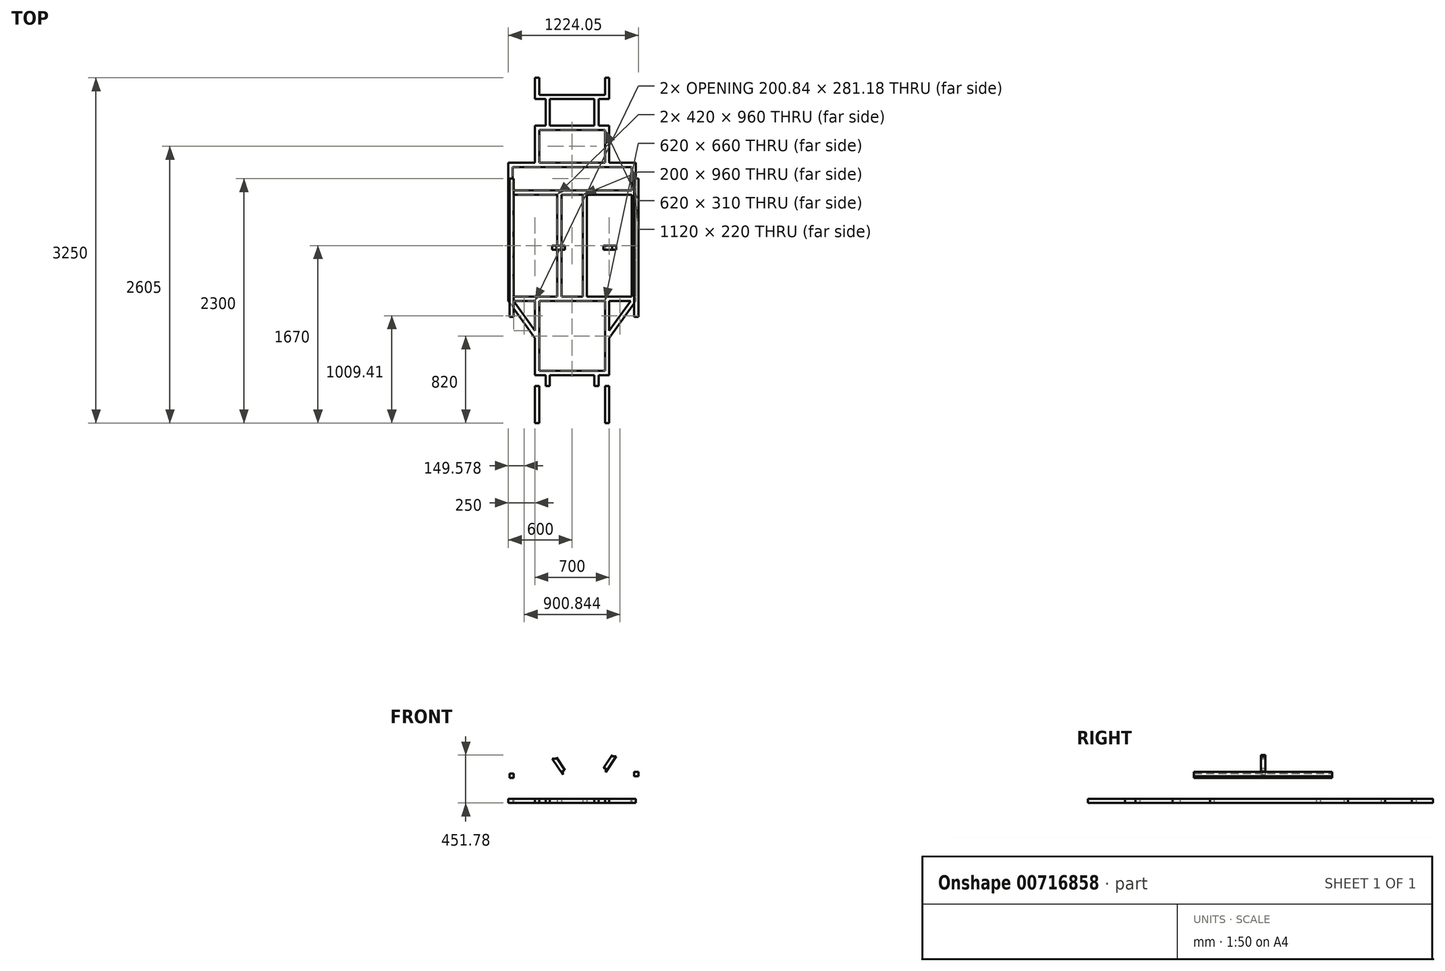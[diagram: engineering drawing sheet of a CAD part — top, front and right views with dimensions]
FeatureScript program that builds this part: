
annotation { "Feature Type Name" : "Feature", "Feature Type Description" : "" }
export const myFeature = defineFeature(function(context is Context, id is Id, definition is map)
    precondition{}
    {
        {
            var Q0;
            Q0=qCreatedBy(makeId("Top.planeOp"),FACE);
            var sketch = newSketch(context, id + "F0", { "sketchPlane" : qUnion([Q0])});
            skLineSegment(sketch, "E0.bottom", {"start": v(100, 500) * mm, "end": v(-100, 500) * mm});
            skLineSegment(sketch, "E0.top", {"start": v(100, -500) * mm, "end": v(-100, -500) * mm});
            skLineSegment(sketch, "E0.right", {"start": v(-100, 500) * mm, "end": v(-100, -460) * mm});
            skPoint(sketch, "E0.middle", {"position": v(0, 0) * mm});
            skLineSegment(sketch, "E1.bottom", {"start": v(140, 500) * mm, "end": v(600, 500) * mm});
            skLineSegment(sketch, "E1.top", {"start": v(100, -500) * mm, "end": v(310, -500) * mm});
            skLineSegment(sketch, "E1.right", {"start": v(600, 500) * mm, "end": v(600, -500) * mm});
            skLineSegment(sketch, "E2.bottom", {"start": v(-140, 500) * mm, "end": v(-560, 500) * mm});
            skLineSegment(sketch, "E2.top", {"start": v(-100, -500) * mm, "end": v(-550.84, -500) * mm});
            skLineSegment(sketch, "E2.right", {"start": v(-600, 500) * mm, "end": v(-600, -500) * mm});
            skLineSegment(sketch, "E3.bottom", {"start": v(-560, 500) * mm, "end": v(-140, 500) * mm});
            skLineSegment(sketch, "E3.top", {"start": v(-600, 800) * mm, "end": v(-350, 800) * mm});
            skLineSegment(sketch, "E3.left", {"start": v(-600, 500) * mm, "end": v(-600, 800) * mm});
            skLineSegment(sketch, "E3.right", {"start": v(600, 500) * mm, "end": v(600, 800) * mm});
            skPoint(sketch, "E4.oppositeSnap0", {"position": v(-350, -500) * mm});
            skLineSegment(sketch, "E4.bottom", {"start": v(0, -500) * mm, "end": v(-350, -500) * mm});
            skLineSegment(sketch, "E4.top", {"start": v(0, -1200) * mm, "end": v(-350, -1200) * mm});
            skLineSegment(sketch, "E4.right", {"start": v(-350, -500) * mm, "end": v(-350, -781.18) * mm});
            skLineSegment(sketch, "E5.bottom", {"start": v(0, -500) * mm, "end": v(310, -500) * mm});
            skLineSegment(sketch, "E5.top", {"start": v(0, -1200) * mm, "end": v(210, -1200) * mm});
            skLineSegment(sketch, "E5.right", {"start": v(350, -500) * mm, "end": v(350, -781.18) * mm});
            skLineSegment(sketch, "E6", {"start": v(-600, -500) * mm, "end": v(-350, -850) * mm});
            skLineSegment(sketch, "E7", {"start": v(-350, -850) * mm, "end": v(-310, -850) * mm});
            skLineSegment(sketch, "E8", {"start": v(350, -850) * mm, "end": v(600, -500) * mm});
            skLineSegment(sketch, "E9.bottom", {"start": v(0, -1200) * mm, "end": v(-250, -1200) * mm});
            skLineSegment(sketch, "E9.top", {"start": v(0, -1300) * mm, "end": v(-250, -1300) * mm});
            skLineSegment(sketch, "E9.right", {"start": v(-250, -1200) * mm, "end": v(-250, -1300) * mm});
            skLineSegment(sketch, "E10.bottom", {"start": v(0, -1200) * mm, "end": v(250, -1200) * mm});
            skLineSegment(sketch, "E10.top", {"start": v(0, -1300) * mm, "end": v(250, -1300) * mm});
            skLineSegment(sketch, "E10.left", {"start": v(0, -1200) * mm, "end": v(0, -1300) * mm});
            skLineSegment(sketch, "E10.right", {"start": v(250, -1200) * mm, "end": v(250, -1300) * mm});
            skLineSegment(sketch, "E11.bottom", {"start": v(0, -1300) * mm, "end": v(-350, -1300) * mm});
            skLineSegment(sketch, "E11.top", {"start": v(-310, -1650) * mm, "end": v(-350, -1650) * mm});
            skLineSegment(sketch, "E11.right", {"start": v(-350, -1300) * mm, "end": v(-350, -1650) * mm});
            skLineSegment(sketch, "E12.bottom", {"start": v(0, -1300) * mm, "end": v(350, -1300) * mm});
            skLineSegment(sketch, "E12.top", {"start": v(310, -1650) * mm, "end": v(350, -1650) * mm});
            skLineSegment(sketch, "E12.right", {"start": v(350, -1300) * mm, "end": v(350, -1650) * mm});
            skLineSegment(sketch, "E13.top", {"start": v(0, 1400) * mm, "end": v(-210, 1400) * mm});
            skLineSegment(sketch, "E14.top", {"start": v(0, 1150) * mm, "end": v(-210, 1150) * mm});
            skLineSegment(sketch, "E14.right", {"start": v(-250, 1400) * mm, "end": v(-250, 1150) * mm});
            skLineSegment(sketch, "E15.bottom", {"start": v(0, 1400) * mm, "end": v(210, 1400) * mm});
            skLineSegment(sketch, "E15.top", {"start": v(0, 1150) * mm, "end": v(210, 1150) * mm});
            skLineSegment(sketch, "E15.right", {"start": v(250, 1400) * mm, "end": v(250, 1150) * mm});
            skLineSegment(sketch, "E16", {"start": v(-250, 1150) * mm, "end": v(-350, 1150) * mm});
            skLineSegment(sketch, "E17", {"start": v(250, 1150) * mm, "end": v(350, 1150) * mm});
            skLineSegment(sketch, "E18.bottom", {"start": v(-350, 1400) * mm, "end": v(-250, 1400) * mm});
            skLineSegment(sketch, "E18.left", {"start": v(-350, 1400) * mm, "end": v(-350, 1600) * mm});
            skLineSegment(sketch, "E18.right", {"start": v(350, 1400) * mm, "end": v(350, 1600) * mm});
            skLineSegment(sketch, "E19", {"start": v(-350, 1150) * mm, "end": v(-350, 800) * mm});
            skLineSegment(sketch, "E20", {"start": v(350, 1150) * mm, "end": v(350, 800) * mm});
            skLineSegment(sketch, "E21.0", {"start": v(310, 1440) * mm, "end": v(310, 1600) * mm});
            skLineSegment(sketch, "E22.0", {"start": v(-310, 1440) * mm, "end": v(-310, 1600) * mm});
            skLineSegment(sketch, "E23.0", {"start": v(-210, 1400) * mm, "end": v(-210, 1150) * mm});
            skLineSegment(sketch, "E24.0", {"start": v(210, 1400) * mm, "end": v(210, 1150) * mm});
            skLineSegment(sketch, "E25.0", {"start": v(310, 1152.57) * mm, "end": v(310, 1150) * mm});
            skLineSegment(sketch, "E26.0", {"start": v(-310, 1110) * mm, "end": v(-310, 800) * mm});
            skLineSegment(sketch, "E27.0", {"start": v(-310, -500) * mm, "end": v(-310, -1160) * mm});
            skLineSegment(sketch, "E28.0", {"start": v(310, -500) * mm, "end": v(310, -1160) * mm});
            skLineSegment(sketch, "E29.0", {"start": v(-210, -1200) * mm, "end": v(-210, -1300) * mm});
            skLineSegment(sketch, "E30.0", {"start": v(210, -1200) * mm, "end": v(210, -1300) * mm});
            skLineSegment(sketch, "E31.0", {"start": v(310, -1300) * mm, "end": v(310, -1650) * mm});
            skLineSegment(sketch, "E32.0", {"start": v(-310, -1300) * mm, "end": v(-310, -1650) * mm});
            skLineSegment(sketch, "E33.trimOffspring", {"start": v(310, -850) * mm, "end": v(350, -850) * mm});
            skLineSegment(sketch, "E34.0", {"start": v(-140, -460) * mm, "end": v(-560, -460) * mm});
            skLineSegment(sketch, "E35.0", {"start": v(140, -460) * mm, "end": v(560, -460) * mm});
            skLineSegment(sketch, "E36.0", {"start": v(100, -460) * mm, "end": v(-100, -460) * mm});
            skLineSegment(sketch, "E37.0", {"start": v(350, -781.18) * mm, "end": v(550.84, -500) * mm});
            skLineSegment(sketch, "E38.0", {"start": v(-550.84, -500) * mm, "end": v(-350, -781.18) * mm});
            skLineSegment(sketch, "E39.0", {"start": v(0, -1160) * mm, "end": v(-310, -1160) * mm});
            skLineSegment(sketch, "E39.1", {"start": v(0, -1160) * mm, "end": v(310, -1160) * mm});
            skLineSegment(sketch, "E40.0", {"start": v(0, -1340) * mm, "end": v(350, -1340) * mm});
            skLineSegment(sketch, "E40.1", {"start": v(0, -1340) * mm, "end": v(-350, -1340) * mm});
            skLineSegment(sketch, "E41.0", {"start": v(-560, 500) * mm, "end": v(-560, -460) * mm});
            skLineSegment(sketch, "E41.1", {"start": v(-560, 540) * mm, "end": v(-560, 760) * mm});
            skLineSegment(sketch, "E42.0", {"start": v(560, 500) * mm, "end": v(560, -460) * mm});
            skLineSegment(sketch, "E43.0", {"start": v(560, 540) * mm, "end": v(560, 760) * mm});
            skLineSegment(sketch, "E44.0", {"start": v(-560, 760) * mm, "end": v(560, 760) * mm});
            skLineSegment(sketch, "E45.0", {"start": v(140, 500) * mm, "end": v(140, -460) * mm});
            skLineSegment(sketch, "E46.0", {"start": v(-140, 500) * mm, "end": v(-140, -460) * mm});
            skLineSegment(sketch, "E47.0", {"start": v(-560, 540) * mm, "end": v(560, 540) * mm});
            skLineSegment(sketch, "E48.trimOffspring", {"start": v(140, 500) * mm, "end": v(560, 500) * mm});
            skLineSegment(sketch, "E49.trimOffspring", {"start": v(-100, 500) * mm, "end": v(100, 500) * mm});
            skLineSegment(sketch, "E50", {"start": v(100, 500) * mm, "end": v(100, -460) * mm});
            skLineSegment(sketch, "E51.bottom", {"start": v(-310, 1150) * mm, "end": v(-250, 1150) * mm});
            skLineSegment(sketch, "E51.top", {"start": v(-310, 1110) * mm, "end": v(310, 1110) * mm});
            skLineSegment(sketch, "E52.bottom", {"start": v(-310, 1400) * mm, "end": v(-250, 1400) * mm});
            skLineSegment(sketch, "E52.top", {"start": v(-310, 1440) * mm, "end": v(310, 1440) * mm});
            skLineSegment(sketch, "E53.trimOffspring", {"start": v(350, -500) * mm, "end": v(550.84, -500) * mm});
            skLineSegment(sketch, "E54.trimOffspring", {"start": v(350, -850) * mm, "end": v(350, -1200) * mm});
            skLineSegment(sketch, "E55.trimOffspring", {"start": v(-350, -850) * mm, "end": v(-350, -1200) * mm});
            skLineSegment(sketch, "E56.trimOffspring", {"start": v(250, -1200) * mm, "end": v(350, -1200) * mm});
            skLineSegment(sketch, "E57.trimOffspring", {"start": v(350, 800) * mm, "end": v(600, 800) * mm});
            skPoint(sketch, "E13.bottom.start.orphan", {"position": v(0, 800) * mm});
            skLineSegment(sketch, "E58.trimOffspring", {"start": v(310, 1110) * mm, "end": v(310, 800) * mm});
            skLineSegment(sketch, "E59.trimOffspring", {"start": v(-210, 1150) * mm, "end": v(210, 1150) * mm});
            skLineSegment(sketch, "E60.trimOffspring", {"start": v(250, 1150) * mm, "end": v(310, 1150) * mm});
            skLineSegment(sketch, "E61", {"start": v(-310, 800) * mm, "end": v(310, 800) * mm});
            skLineSegment(sketch, "E62.trimOffspring", {"start": v(250, 1400) * mm, "end": v(350, 1400) * mm});
            skLineSegment(sketch, "E63.trimOffspring", {"start": v(250, 1400) * mm, "end": v(310, 1400) * mm});
            skLineSegment(sketch, "E64.trimOffspring", {"start": v(-210, 1400) * mm, "end": v(210, 1400) * mm});
            skLineSegment(sketch, "E65.trimOffspring", {"start": v(-250, 1400) * mm, "end": v(-350, 1400) * mm});
            skLineSegment(sketch, "E66", {"start": v(-350, 1600) * mm, "end": v(-310, 1600) * mm});
            skLineSegment(sketch, "E67", {"start": v(310, 1600) * mm, "end": v(350, 1600) * mm});
            skSolve(sketch);
        }
        {
            var Q0;
            Q0=makeQuery(id+"F0.imprint","IMPRINT",FACE,{"disambiguationData":[TD([[makeQuery(id+"F0.imprint","IMPRINT",EDGE,{"derivedFrom":sQuery(id+"F0.wireOp",EDGE,"E0.right")}),-1.0]])]});
            var Q1;
            {var subQ11=sQuery(id+"F0.wireOp",EDGE,"E4.top");Q1=makeQuery(id+"F0.imprint","IMPRINT",FACE,{"disambiguationData":[TD([[makeQuery(id+"F0.imprint","IMPRINT",EDGE,{"derivedFrom":subQ11}),-1.0]])]});}
            var Q2;
            {var subQ0=sQuery(id+"F0.wireOp",EDGE,"E10.right");Q2=makeQuery(id+"F0.imprint","IMPRINT",FACE,{"disambiguationData":[TD([[makeQuery(id+"F0.imprint","IMPRINT",EDGE,{"derivedFrom":subQ0}),-1.0]])]});}
            var Q3;
            {var subQ0=sQuery(id+"F0.wireOp",EDGE,"E9.right");Q3=makeQuery(id+"F0.imprint","IMPRINT",FACE,{"disambiguationData":[TD([[makeQuery(id+"F0.imprint","IMPRINT",EDGE,{"derivedFrom":subQ0}),1.0]])]});}
            var Q4;
            {var subQ1=sQuery(id+"F0.wireOp",EDGE,"E11.bottom");var subQ9=makeQuery(id+"F0.imprint","INTERSECT",VERTEX,{"derivedFrom":[sQuery(id+"F0.wireOp",EDGE,"E9.right"),subQ1]});Q4=makeQuery(id+"F0.imprint","IMPRINT",FACE,{"disambiguationData":[TD([[makeQuery(id+"F0.imprint","IMPRINT",EDGE,{"disambiguationData":[TD([[subQ9,1.0]])],"derivedFrom":subQ1}),1.0]])]});}
            var Q5;
            {var subQ0=sQuery(id+"F0.wireOp",EDGE,"E12.top");Q5=makeQuery(id+"F0.imprint","IMPRINT",FACE,{"disambiguationData":[TD([[makeQuery(id+"F0.imprint","IMPRINT",EDGE,{"derivedFrom":subQ0}),1.0]])]});}
            var Q6;
            {var subQ0=sQuery(id+"F0.wireOp",EDGE,"E11.top");Q6=makeQuery(id+"F0.imprint","IMPRINT",FACE,{"disambiguationData":[TD([[makeQuery(id+"F0.imprint","IMPRINT",EDGE,{"derivedFrom":subQ0}),-1.0]])]});}
            var Q7;
            {var subQ0=sQuery(id+"F0.wireOp",EDGE,"E11.right");var subQ1=sQuery(id+"F0.wireOp",EDGE,"E11.bottom");var subQ2=makeQuery(id+"F0.imprint","INTERSECT",VERTEX,{"derivedFrom":[subQ1,subQ0]});Q7=makeQuery(id+"F0.imprint","IMPRINT",FACE,{"disambiguationData":[TD([[makeQuery(id+"F0.imprint","IMPRINT",EDGE,{"disambiguationData":[TD([[subQ2,1.0]])],"derivedFrom":subQ1}),1.0]])]});}
            var Q8;
            {var subQ0=sQuery(id+"F0.wireOp",EDGE,"E12.right");var subQ1=sQuery(id+"F0.wireOp",EDGE,"E12.bottom");var subQ2=makeQuery(id+"F0.imprint","INTERSECT",VERTEX,{"derivedFrom":[subQ1,subQ0]});Q8=makeQuery(id+"F0.imprint","IMPRINT",FACE,{"disambiguationData":[TD([[makeQuery(id+"F0.imprint","IMPRINT",EDGE,{"disambiguationData":[TD([[subQ2,1.0]])],"derivedFrom":subQ1}),-1.0]])]});}
            extrude(context, id + "F1", {"entities" : qUnion([Q0, Q1, Q2, Q3, Q4, Q5, Q6, Q7, Q8]), "endBound" : BoundingType.SYMMETRIC, "depth" : 40 * mm, "offsetDistance" : 25 * mm});
        }
        {
            var Q0;
            Q0=qCreatedBy(makeId("Front.planeOp"),FACE);
            var sketch = newSketch(context, id + "F2", { "sketchPlane" : qUnion([Q0])});
            skLineSegment(sketch, "E68.bottom", {"start": v(-588.94, 217.43) * mm, "end": v(-548.94, 217.43) * mm});
            skLineSegment(sketch, "E68.top", {"start": v(-588.94, 257.43) * mm, "end": v(-548.94, 257.43) * mm});
            skLineSegment(sketch, "E68.left", {"start": v(-588.94, 217.43) * mm, "end": v(-588.94, 257.43) * mm});
            skLineSegment(sketch, "E68.right", {"start": v(-548.94, 217.43) * mm, "end": v(-548.94, 257.43) * mm});
            skPoint(sketch, "E68.middle", {"position": v(-568.94, 237.43) * mm});
            skSolve(sketch);
        }
        {
            var Q0;
            Q0 = qSketchRegion(id + "F2", true);
            extrude(context, id + "F3", {"entities" : qUnion([Q0]), "endBound" : BoundingType.SYMMETRIC, "depth" : 1300 * mm, "offsetDistance" : 25 * mm});
        }
        {
            var Q0;
            Q0=qCreatedBy(makeId("Front.planeOp"),FACE);
            var sketch = newSketch(context, id + "F4", { "sketchPlane" : qUnion([Q0])});
            skLineSegment(sketch, "E69.bottom", {"start": v(584.05, 271.92) * mm, "end": v(624.05, 271.92) * mm});
            skLineSegment(sketch, "E69.top", {"start": v(584.05, 231.92) * mm, "end": v(624.05, 231.92) * mm});
            skLineSegment(sketch, "E69.left", {"start": v(584.05, 271.92) * mm, "end": v(584.05, 231.92) * mm});
            skLineSegment(sketch, "E69.right", {"start": v(624.05, 271.92) * mm, "end": v(624.05, 231.92) * mm});
            skPoint(sketch, "E69.middle", {"position": v(604.05, 251.92) * mm});
            skSolve(sketch);
        }
        {
            var Q0;
            Q0 = qSketchRegion(id + "F4", true);
            extrude(context, id + "F5", {"entities" : qUnion([Q0]), "endBound" : BoundingType.SYMMETRIC, "depth" : 1300 * mm, "offsetDistance" : 25 * mm});
        }
        {
            var Q0;
            Q0=qCreatedBy(makeId("Front.planeOp"),FACE);
            var sketch = newSketch(context, id + "F6", { "sketchPlane" : qUnion([Q0])});
            skLineSegment(sketch, "E70.top", {"start": v(416.08, 419.67) * mm, "end": v(376.08, 419.67) * mm});
            skLineSegment(sketch, "E70.right", {"start": v(376.08, 431.78) * mm, "end": v(376.08, 419.67) * mm});
            skLineSegment(sketch, "E71.top", {"start": v(294.68, 309.67) * mm, "end": v(316.08, 309.67) * mm});
            skLineSegment(sketch, "E71.right", {"start": v(316.08, 269.67) * mm, "end": v(316.08, 309.67) * mm});
            skLineSegment(sketch, "E72", {"start": v(416.08, 419.67) * mm, "end": v(316.08, 269.67) * mm});
            skLineSegment(sketch, "E73.0", {"start": v(376.08, 431.78) * mm, "end": v(294.68, 309.67) * mm});
            skSolve(sketch);
        }
        {
            var Q0;
            Q0=makeQuery(id+"F6.imprint","IMPRINT",FACE,{"disambiguationData":[TD([[makeQuery(id+"F6.imprint","IMPRINT",EDGE,{"derivedFrom":sQuery(id+"F6.wireOp",EDGE,"E70.top")}),1.0]])]});
            extrude(context, id + "F7", {"entities" : qUnion([Q0]), "endBound" : BoundingType.SYMMETRIC, "depth" : 40 * mm, "offsetDistance" : 25 * mm});
        }
        {
            var Q0;
            Q0=qCreatedBy(makeId("Front.planeOp"),FACE);
            var sketch = newSketch(context, id + "F8", { "sketchPlane" : qUnion([Q0])});
            skLineSegment(sketch, "E74.top", {"start": v(-187.5, 398.23) * mm, "end": v(-147.5, 398.23) * mm});
            skLineSegment(sketch, "E74.right", {"start": v(-147.5, 410.35) * mm, "end": v(-147.5, 398.23) * mm});
            skLineSegment(sketch, "E75.top", {"start": v(-66.1, 288.23) * mm, "end": v(-87.5, 288.23) * mm});
            skLineSegment(sketch, "E75.right", {"start": v(-87.5, 248.23) * mm, "end": v(-87.5, 288.23) * mm});
            skLineSegment(sketch, "E76", {"start": v(-187.5, 398.23) * mm, "end": v(-87.5, 248.23) * mm});
            skLineSegment(sketch, "E77.0", {"start": v(-147.5, 410.35) * mm, "end": v(-66.1, 288.23) * mm});
            skSolve(sketch);
        }
        {
            var Q0;
            Q0 = qSketchRegion(id + "F8", true);
            extrude(context, id + "F9", {"entities" : qUnion([Q0]), "endBound" : BoundingType.SYMMETRIC, "depth" : 40 * mm, "offsetDistance" : 25 * mm});
        }
    });
